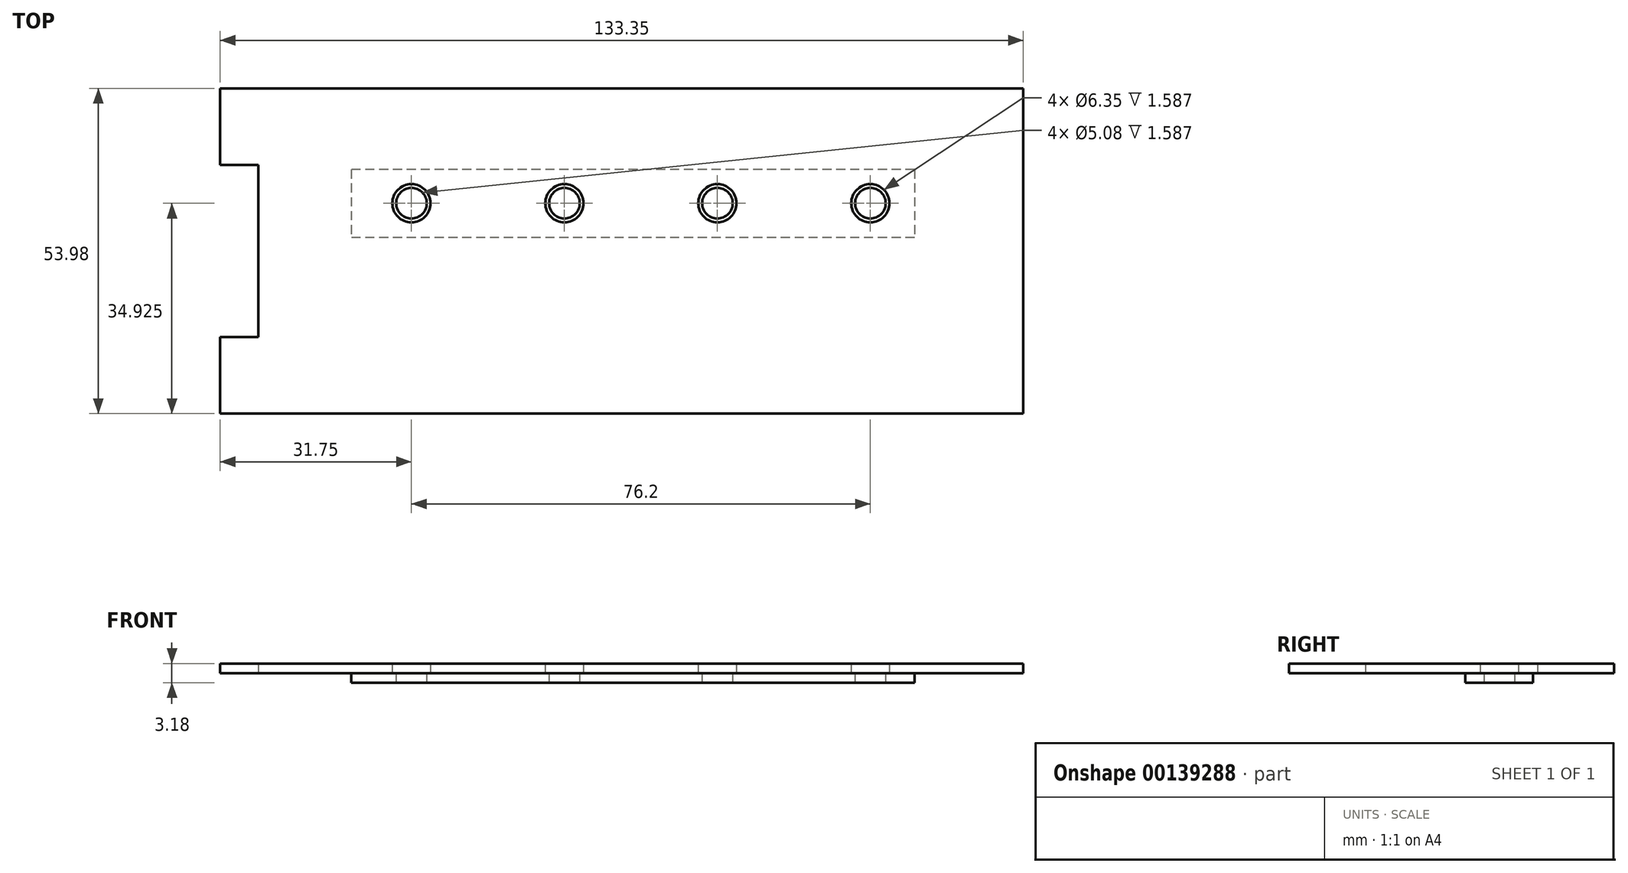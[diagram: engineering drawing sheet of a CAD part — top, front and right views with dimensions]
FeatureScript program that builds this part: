
annotation { "Feature Type Name" : "Feature", "Feature Type Description" : "" }
export const myFeature = defineFeature(function(context is Context, id is Id, definition is map)
    precondition{}
    {
        {
            var Q0;
            Q0=qCreatedBy(makeId("Top.planeOp"),FACE);
            var sketch = newSketch(context, id + "F0", { "sketchPlane" : qUnion([Q0])});
            skLineSegment(sketch, "E0.bottom", {"start": v(0, 0) * mm, "end": v(127, 0) * mm});
            skLineSegment(sketch, "E0.top", {"start": v(0, 53.98) * mm, "end": v(127, 53.98) * mm});
            skLineSegment(sketch, "E0.left", {"start": v(0, 0) * mm, "end": v(0, 53.98) * mm});
            skLineSegment(sketch, "E0.right", {"start": v(127, 0) * mm, "end": v(127, 53.98) * mm});
            skLineSegment(sketch, "E1", {"start": v(0, 0) * mm, "end": v(0, 34.93) * mm});
            skLineSegment(sketch, "E2", {"start": v(0, 34.93) * mm, "end": v(127, 34.93) * mm});
            skCircle(sketch, "E3", {"center": v(25.4, 34.93) * mm, "radius": 3.18 * mm});
            skCircle(sketch, "E4", {"center": v(50.8, 34.93) * mm, "radius": 3.18 * mm});
            skCircle(sketch, "E5", {"center": v(76.2, 34.93) * mm, "radius": 3.17 * mm});
            skCircle(sketch, "E6", {"center": v(101.6, 34.93) * mm, "radius": 3.18 * mm});
            skLineSegment(sketch, "E7.bottom", {"start": v(0, 0) * mm, "end": v(-6.35, 0) * mm});
            skLineSegment(sketch, "E7.top", {"start": v(0, 12.7) * mm, "end": v(-6.35, 12.7) * mm});
            skLineSegment(sketch, "E7.left", {"start": v(0, 0) * mm, "end": v(0, 12.7) * mm});
            skLineSegment(sketch, "E7.right", {"start": v(-6.35, 0) * mm, "end": v(-6.35, 12.7) * mm});
            skLineSegment(sketch, "E8.bottom", {"start": v(0, 53.98) * mm, "end": v(-6.35, 53.98) * mm});
            skLineSegment(sketch, "E8.top", {"start": v(0, 41.27) * mm, "end": v(-6.35, 41.27) * mm});
            skLineSegment(sketch, "E8.left", {"start": v(0, 53.98) * mm, "end": v(0, 41.27) * mm});
            skLineSegment(sketch, "E8.right", {"start": v(-6.35, 53.98) * mm, "end": v(-6.35, 41.27) * mm});
            skLineSegment(sketch, "E9.bottom", {"start": v(127, 53.98) * mm, "end": v(133.35, 53.98) * mm});
            skLineSegment(sketch, "E9.top", {"start": v(127, 41.27) * mm, "end": v(133.35, 41.27) * mm});
            skLineSegment(sketch, "E9.left", {"start": v(127, 53.98) * mm, "end": v(127, 41.27) * mm});
            skLineSegment(sketch, "E9.right", {"start": v(133.35, 53.98) * mm, "end": v(133.35, 41.28) * mm});
            skLineSegment(sketch, "E10.bottom", {"start": v(127, 0) * mm, "end": v(133.35, 0) * mm});
            skLineSegment(sketch, "E10.top", {"start": v(127, 12.7) * mm, "end": v(133.35, 12.7) * mm});
            skLineSegment(sketch, "E10.left", {"start": v(127, 0) * mm, "end": v(127, 12.7) * mm});
            skLineSegment(sketch, "E10.right", {"start": v(133.35, 0) * mm, "end": v(133.35, 12.7) * mm});
            skLineSegment(sketch, "E11.bottom", {"start": v(133.35, 41.27) * mm, "end": v(127, 41.27) * mm});
            skLineSegment(sketch, "E11.top", {"start": v(133.35, 12.7) * mm, "end": v(127, 12.7) * mm});
            skLineSegment(sketch, "E11.left", {"start": v(133.35, 41.27) * mm, "end": v(133.35, 12.7) * mm});
            skLineSegment(sketch, "E11.right", {"start": v(127, 41.27) * mm, "end": v(127, 12.7) * mm});
            skSolve(sketch);
        }
        {
            var Q0;
            Q0=makeQuery(id+"F0.imprint","IMPRINT",FACE,{"disambiguationData":[TD([[makeQuery(id+"F0.imprint","IMPRINT",EDGE,{"derivedFrom":sQuery(id+"F0.wireOp",EDGE,"E0.bottom")}),1.0]])]});
            var Q1;
            Q1=makeQuery(id+"F0.imprint","IMPRINT",FACE,{"disambiguationData":[TD([[makeQuery(id+"F0.imprint","IMPRINT",EDGE,{"derivedFrom":sQuery(id+"F0.wireOp",EDGE,"E7.bottom")}),-1.0]])]});
            var Q2;
            Q2=makeQuery(id+"F0.imprint","IMPRINT",FACE,{"disambiguationData":[TD([[makeQuery(id+"F0.imprint","IMPRINT",EDGE,{"derivedFrom":sQuery(id+"F0.wireOp",EDGE,"E8.bottom")}),1.0]])]});
            var Q3;
            Q3=makeQuery(id+"F0.imprint","IMPRINT",FACE,{"disambiguationData":[TD([[makeQuery(id+"F0.imprint","IMPRINT",EDGE,{"derivedFrom":sQuery(id+"F0.wireOp",EDGE,"E0.top")}),-1.0]])]});
            var Q4;
            {var subQ2=sQuery(id+"F0.wireOp",EDGE,"E11.bottom");Q4=makeQuery(id+"F0.imprint","IMPRINT",FACE,{"disambiguationData":[TD([[makeQuery(id+"F0.imprint","IMPRINT",EDGE,{"derivedFrom":subQ2}),1.0]])]});}
            extrude(context, id + "F1", {"entities" : qUnion([Q0, Q1, Q2, Q3, Q4]), "depth" : 1.59 * mm});
        }
        {
            var Q0;
            Q0=makeQuery(id+"F1.opExtrude","CAP_FACE",FACE,{"disambiguationData":[OSD([sQuery(id+"F0.wireOp",EDGE,"E0.bottom"),sQuery(id+"F0.wireOp",EDGE,"E0.top"),sQuery(id+"F0.wireOp",EDGE,"E0.left"),sQuery(id+"F0.wireOp",EDGE,"E1"),sQuery(id+"F0.wireOp",EDGE,"E3"),sQuery(id+"F0.wireOp",EDGE,"E4"),sQuery(id+"F0.wireOp",EDGE,"E5"),sQuery(id+"F0.wireOp",EDGE,"E6"),sQuery(id+"F0.wireOp",EDGE,"E7.bottom"),sQuery(id+"F0.wireOp",EDGE,"E7.top"),sQuery(id+"F0.wireOp",EDGE,"E7.right"),sQuery(id+"F0.wireOp",EDGE,"E8.bottom"),sQuery(id+"F0.wireOp",EDGE,"E8.top"),sQuery(id+"F0.wireOp",EDGE,"E8.right"),sQuery(id+"F0.wireOp",EDGE,"E9.left"),sQuery(id+"F0.wireOp",EDGE,"E10.left"),sQuery(id+"F0.wireOp",EDGE,"E11.bottom"),sQuery(id+"F0.wireOp",EDGE,"E11.top"),sQuery(id+"F0.wireOp",EDGE,"E11.left")])],"isStart":true});
            var sketch = newSketch(context, id + "F2", { "sketchPlane" : qUnion([Q0])});
            skLineSegment(sketch, "E12.bottom", {"start": v(108.94, -40.5) * mm, "end": v(15.43, -40.5) * mm});
            skLineSegment(sketch, "E12.top", {"start": v(108.94, -29.24) * mm, "end": v(15.43, -29.24) * mm});
            skLineSegment(sketch, "E12.left", {"start": v(108.94, -40.5) * mm, "end": v(108.94, -29.24) * mm});
            skLineSegment(sketch, "E12.right", {"start": v(15.43, -40.5) * mm, "end": v(15.43, -29.24) * mm});
            skSolve(sketch);
        }
        {
            var Q0;
            Q0=makeQuery(id+"F2.imprint","IMPRINT",FACE,{"disambiguationData":[TD([[makeQuery(id+"F2.imprint","IMPRINT",EDGE,{"derivedFrom":sQuery(id+"F2.wireOp",EDGE,"E12.bottom")}),-1.0]])]});
            extrude(context, id + "F3", {"entities" : qUnion([Q0]), "operationType" : NewBodyOperationType.ADD, "depth" : 1.59 * mm});
        }
        {
            var Q0;
            Q0=makeQuery(id+"F3.opExtrude","CAP_FACE",FACE,{"disambiguationData":[OSD([sQuery(id+"F0.wireOp",EDGE,"E3"),sQuery(id+"F0.wireOp",EDGE,"E4"),sQuery(id+"F0.wireOp",EDGE,"E5"),sQuery(id+"F0.wireOp",EDGE,"E6"),sQuery(id+"F2.wireOp",EDGE,"E12.bottom"),sQuery(id+"F2.wireOp",EDGE,"E12.top"),sQuery(id+"F2.wireOp",EDGE,"E12.left"),sQuery(id+"F2.wireOp",EDGE,"E12.right")])],"isStart":false});
            var sketch = newSketch(context, id + "F4", { "sketchPlane" : qUnion([Q0])});
            skCircle(sketch, "E13", {"center": v(101.6, -34.93) * mm, "radius": 2.54 * mm});
            skCircle(sketch, "E14", {"center": v(101.6, -34.93) * mm, "radius": 3.18 * mm});
            skCircle(sketch, "E15", {"center": v(76.2, -34.93) * mm, "radius": 2.54 * mm});
            skCircle(sketch, "E16", {"center": v(76.2, -34.93) * mm, "radius": 3.18 * mm});
            skCircle(sketch, "E17", {"center": v(50.8, -34.93) * mm, "radius": 2.54 * mm});
            skCircle(sketch, "E18", {"center": v(50.8, -34.93) * mm, "radius": 3.18 * mm});
            skCircle(sketch, "E19", {"center": v(25.4, -34.93) * mm, "radius": 2.54 * mm});
            skCircle(sketch, "E20", {"center": v(25.4, -34.93) * mm, "radius": 3.18 * mm});
            skSolve(sketch);
        }
        {
            var Q0;
            Q0=makeQuery(id+"F4.imprint","IMPRINT",FACE,{"disambiguationData":[TD([[makeQuery(id+"F4.imprint","IMPRINT",EDGE,{"derivedFrom":sQuery(id+"F4.wireOp",EDGE,"E13")}),-1.0]])]});
            var Q1;
            Q1=makeQuery(id+"F4.imprint","IMPRINT",FACE,{"disambiguationData":[TD([[makeQuery(id+"F4.imprint","IMPRINT",EDGE,{"derivedFrom":sQuery(id+"F4.wireOp",EDGE,"E15")}),-1.0]])]});
            var Q2;
            Q2=makeQuery(id+"F4.imprint","IMPRINT",FACE,{"disambiguationData":[TD([[makeQuery(id+"F4.imprint","IMPRINT",EDGE,{"derivedFrom":sQuery(id+"F4.wireOp",EDGE,"E17")}),-1.0]])]});
            var Q3;
            Q3=makeQuery(id+"F4.imprint","IMPRINT",FACE,{"disambiguationData":[TD([[makeQuery(id+"F4.imprint","IMPRINT",EDGE,{"derivedFrom":sQuery(id+"F4.wireOp",EDGE,"E19")}),-1.0]])]});
            extrude(context, id + "F5", {"entities" : qUnion([Q0, Q1, Q2, Q3]), "operationType" : NewBodyOperationType.ADD, "oppositeDirection" : true, "depth" : 1.59 * mm});
        }
    });
